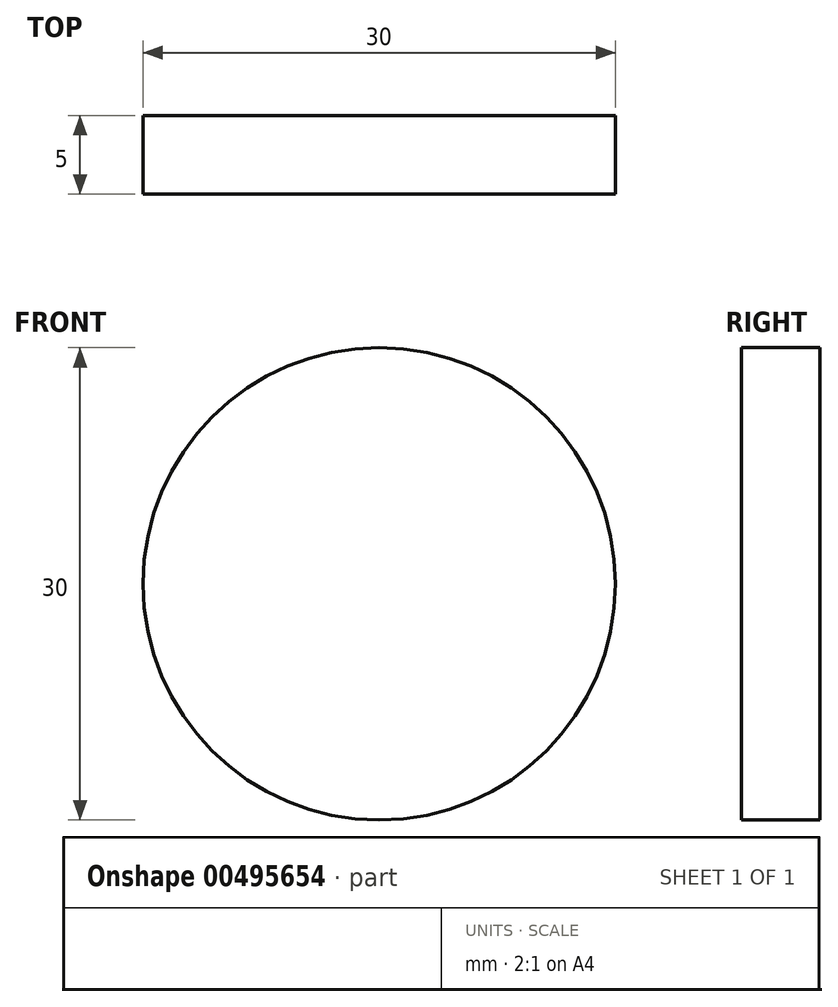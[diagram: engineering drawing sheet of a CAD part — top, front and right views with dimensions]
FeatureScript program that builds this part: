
annotation { "Feature Type Name" : "Feature", "Feature Type Description" : "" }
export const myFeature = defineFeature(function(context is Context, id is Id, definition is map)
    precondition{}
    {
        {
            var Q0;
            Q0=qCreatedBy(makeId("Front.planeOp"),FACE);
            var sketch = newSketch(context, id + "F0", { "sketchPlane" : qUnion([Q0])});
            skCircle(sketch, "E0", {"center": v(0, 0) * mm, "radius": 15 * mm});
            skSolve(sketch);
        }
        {
            var Q0;
            Q0 = qSketchRegion(id + "F0", true);
            extrude(context, id + "F1", {"entities" : qUnion([Q0]), "depth" : 5 * mm});
        }
    });
